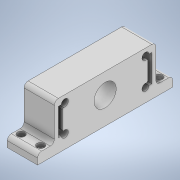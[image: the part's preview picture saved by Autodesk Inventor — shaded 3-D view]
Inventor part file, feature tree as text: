
AUTODESK INVENTOR PART (.ipt)
format: ipt  version: 2020 (Build 240168000, 168)  size: 248,320 bytes
history: native  units: mm
features: extrude x5, other x1, sketch x1, mirror x1
ambient origin geometry x8: Origin, YZ Plane, XZ Plane, XY Plane, X Axis, Y Axis, Z Axis, Center Point
bodies: Body1 (feature_tree)
feature tree (8):
  other  "Bryła1"
  extrude  "Wyciągnięcie proste1"  Depth=33.0mm
  extrude  "Wyciągnięcie proste4"  Depth=10.5mm
  extrude  "Wyciągnięcie proste7"  Depth=40.0mm
  sketch  "Szkic2"
  extrude  "Wyciągnięcie proste5"  Depth=60.0mm
  extrude  "Wyciągnięcie proste6"  Depth=6.0mm
  mirror  "Odbij1"
